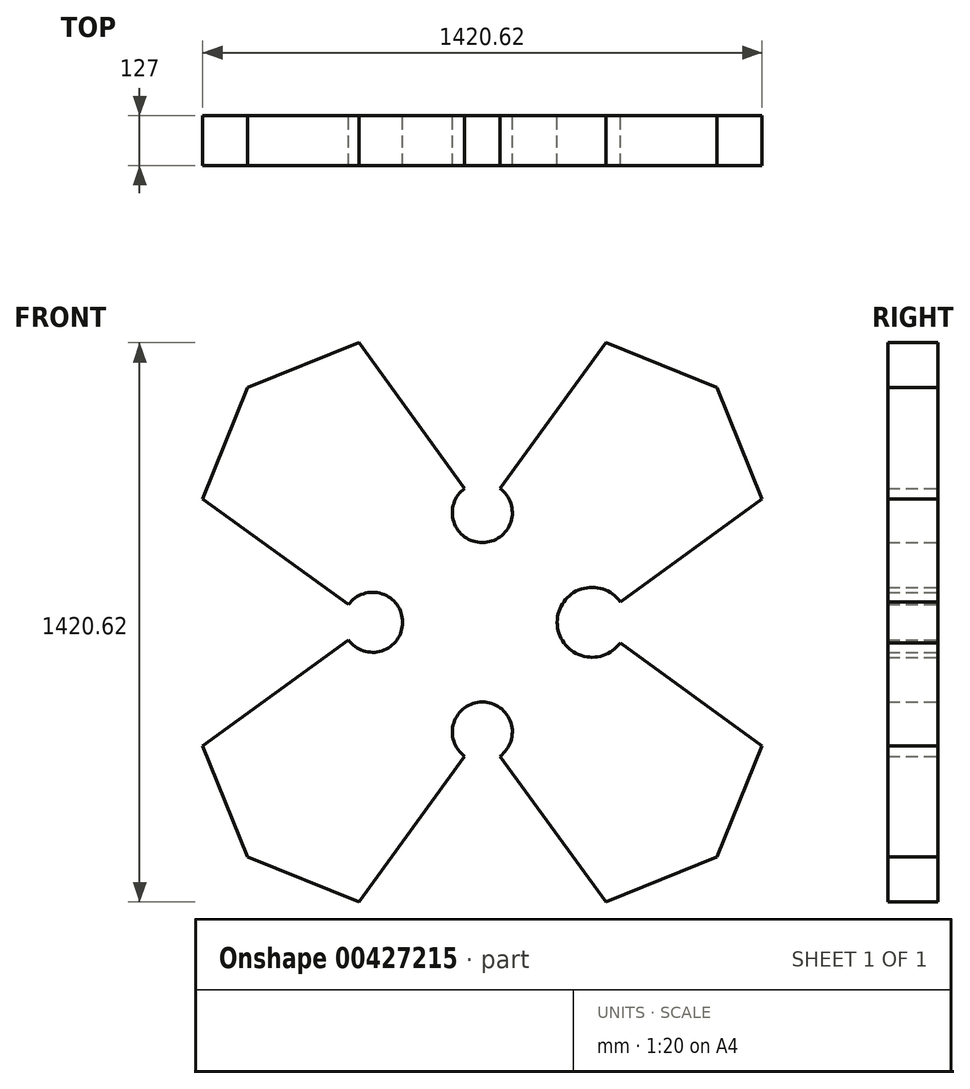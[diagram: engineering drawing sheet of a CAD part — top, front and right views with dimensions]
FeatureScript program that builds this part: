
annotation { "Feature Type Name" : "Feature", "Feature Type Description" : "" }
export const myFeature = defineFeature(function(context is Context, id is Id, definition is map)
    precondition{}
    {
        {
            var Q0;
            Q0=qCreatedBy(makeId("Front.planeOp"),FACE);
            var sketch = newSketch(context, id + "F0", { "sketchPlane" : qUnion([Q0])});
            skLineSegment(sketch, "E0", {"start": v(824.79, 0) * mm, "end": v(1107.4, -114.18) * mm});
            skLineSegment(sketch, "E1", {"start": v(1107.4, -114.18) * mm, "end": v(1376.13, 255.7) * mm});
            skLineSegment(sketch, "E2.MirrorCS", {"start": v(824.79, 0) * mm, "end": v(710.6, 282.6) * mm});
            skLineSegment(sketch, "E3.MirrorCS", {"start": v(710.6, 282.6) * mm, "end": v(1080.49, 551.34) * mm});
            skLineSegment(sketch, "E4.MirrorCS", {"start": v(1734.44, -114.18) * mm, "end": v(1465.7, 255.7) * mm});
            skLineSegment(sketch, "E5.MirrorCS", {"start": v(2017.05, 0) * mm, "end": v(1734.44, -114.18) * mm});
            skArc(sketch, "E6", {"start": v(1465.7, 255.7) * mm, "mid": v(1420.92, 393.55) * mm, "end": v(1376.13, 255.7) * mm});
            skLineSegment(sketch, "E7.MirrorCS", {"start": v(2017.05, 0) * mm, "end": v(2131.23, 282.6) * mm});
            skLineSegment(sketch, "E8.MirrorCS", {"start": v(2131.23, 282.6) * mm, "end": v(1771.55, 543.92) * mm});
            skArc(sketch, "E9", {"start": v(1080.49, 551.34) * mm, "mid": v(1218.33, 596.13) * mm, "end": v(1080.49, 640.92) * mm});
            skArc(sketch, "E10", {"start": v(1771.55, 648.34) * mm, "mid": v(1610.88, 596.13) * mm, "end": v(1771.55, 543.92) * mm});
            skLineSegment(sketch, "E11.MirrorCS", {"start": v(2131.23, 909.65) * mm, "end": v(1771.55, 648.34) * mm});
            skLineSegment(sketch, "E12.MirrorCS", {"start": v(2017.05, 1192.26) * mm, "end": v(2131.23, 909.65) * mm});
            skLineSegment(sketch, "E13.MirrorCS", {"start": v(2017.05, 1192.26) * mm, "end": v(1734.44, 1306.44) * mm});
            skLineSegment(sketch, "E14.MirrorCS", {"start": v(1734.44, 1306.44) * mm, "end": v(1465.7, 936.56) * mm});
            skArc(sketch, "E15.MirrorCS", {"start": v(1465.7, 936.56) * mm, "mid": v(1420.92, 798.71) * mm, "end": v(1376.13, 936.56) * mm});
            skLineSegment(sketch, "E16.MirrorCS", {"start": v(1107.4, 1306.44) * mm, "end": v(1376.13, 936.56) * mm});
            skLineSegment(sketch, "E17.MirrorCS", {"start": v(824.79, 1192.26) * mm, "end": v(1107.4, 1306.44) * mm});
            skLineSegment(sketch, "E18.MirrorCS", {"start": v(824.79, 1192.26) * mm, "end": v(710.6, 909.65) * mm});
            skLineSegment(sketch, "E19.MirrorCS", {"start": v(710.6, 909.65) * mm, "end": v(1080.49, 640.92) * mm});
            skSolve(sketch);
        }
        {
            var Q0;
            Q0=makeQuery(id+"F0.imprint","IMPRINT",FACE,{"disambiguationData":[TD([[makeQuery(id+"F0.imprint","IMPRINT",EDGE,{"derivedFrom":sQuery(id+"F0.wireOp",EDGE,"E0")}),1.0]])]});
            extrude(context, id + "F1", {"entities" : qUnion([Q0]), "depth" : 127 * mm});
        }
    });
